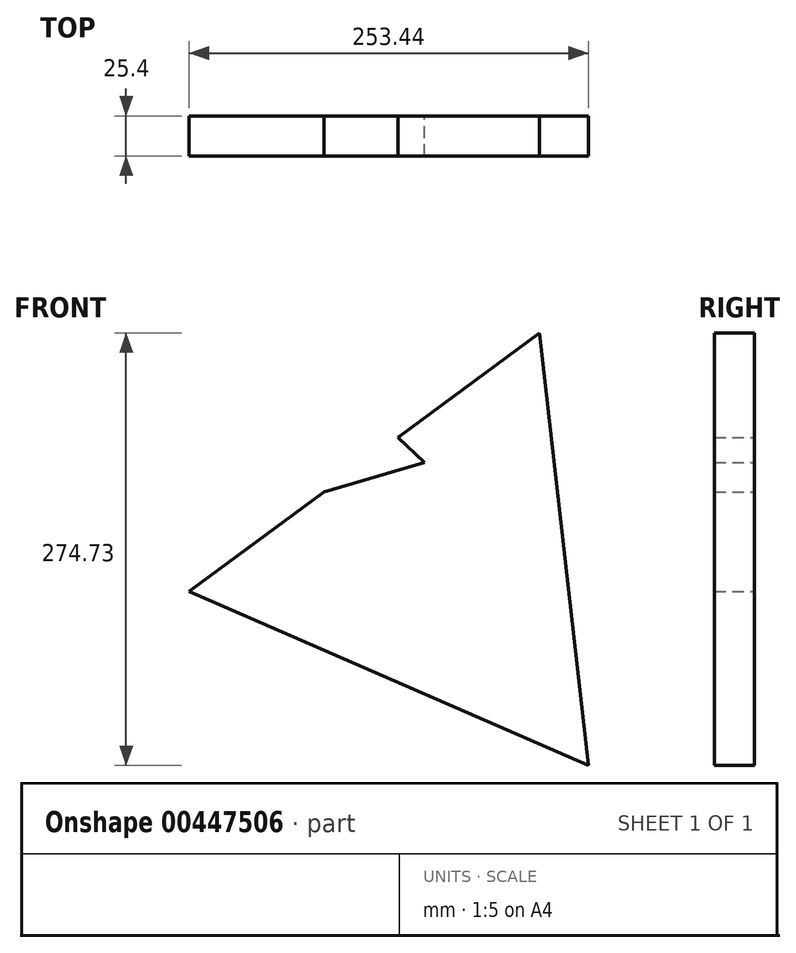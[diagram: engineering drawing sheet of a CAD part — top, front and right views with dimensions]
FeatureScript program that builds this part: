
annotation { "Feature Type Name" : "Feature", "Feature Type Description" : "" }
export const myFeature = defineFeature(function(context is Context, id is Id, definition is map)
    precondition{}
    {
        {
            var Q0;
            Q0=qCreatedBy(makeId("Front.planeOp"),FACE);
            var sketch = newSketch(context, id + "F0", { "sketchPlane" : qUnion([Q0])});
            skCircle(sketch, "E0.cCircle", {"center": v(49.57, 118.96) * mm, "radius": 159.62 * mm, "construction": true});
            skLineSegment(sketch, "E0.0", {"start": v(-109.05, 101.05) * mm, "end": v(113.36, 265.28) * mm});
            skLineSegment(sketch, "E0.1", {"start": v(113.36, 265.28) * mm, "end": v(144.39, -9.45) * mm});
            skLineSegment(sketch, "E0.2", {"start": v(144.39, -9.45) * mm, "end": v(-109.05, 101.05) * mm});
            skCircle(sketch, "E1.cCircle", {"center": v(-10.92, 195.44) * mm, "radius": 52.74 * mm, "construction": true});
            skPoint(sketch, "E1.cCircle.perimeterSnap0", {"position": v(2.16, 183.16) * mm});
            skLineSegment(sketch, "E1.0", {"start": v(40.37, 183.16) * mm, "end": v(-47.2, 157.16) * mm});
            skPoint(sketch, "E1.0.startSnap0", {"position": v(2.16, 183.16) * mm});
            skLineSegment(sketch, "E1.1", {"start": v(-47.2, 157.16) * mm, "end": v(-25.94, 246) * mm});
            skLineSegment(sketch, "E1.2", {"start": v(-25.94, 246) * mm, "end": v(40.37, 183.16) * mm});
            skSolve(sketch);
        }
        {
            var Q0;
            {var subQ1=sQuery(id+"F0.wireOp",EDGE,"E0.1");Q0=makeQuery(id+"F0.imprint","IMPRINT",FACE,{"disambiguationData":[TD([[makeQuery(id+"F0.imprint","IMPRINT",EDGE,{"derivedFrom":subQ1}),-1.0]])]});}
            extrude(context, id + "F1", {"entities" : qUnion([Q0]), "depth" : 25.4 * mm});
        }
    });
